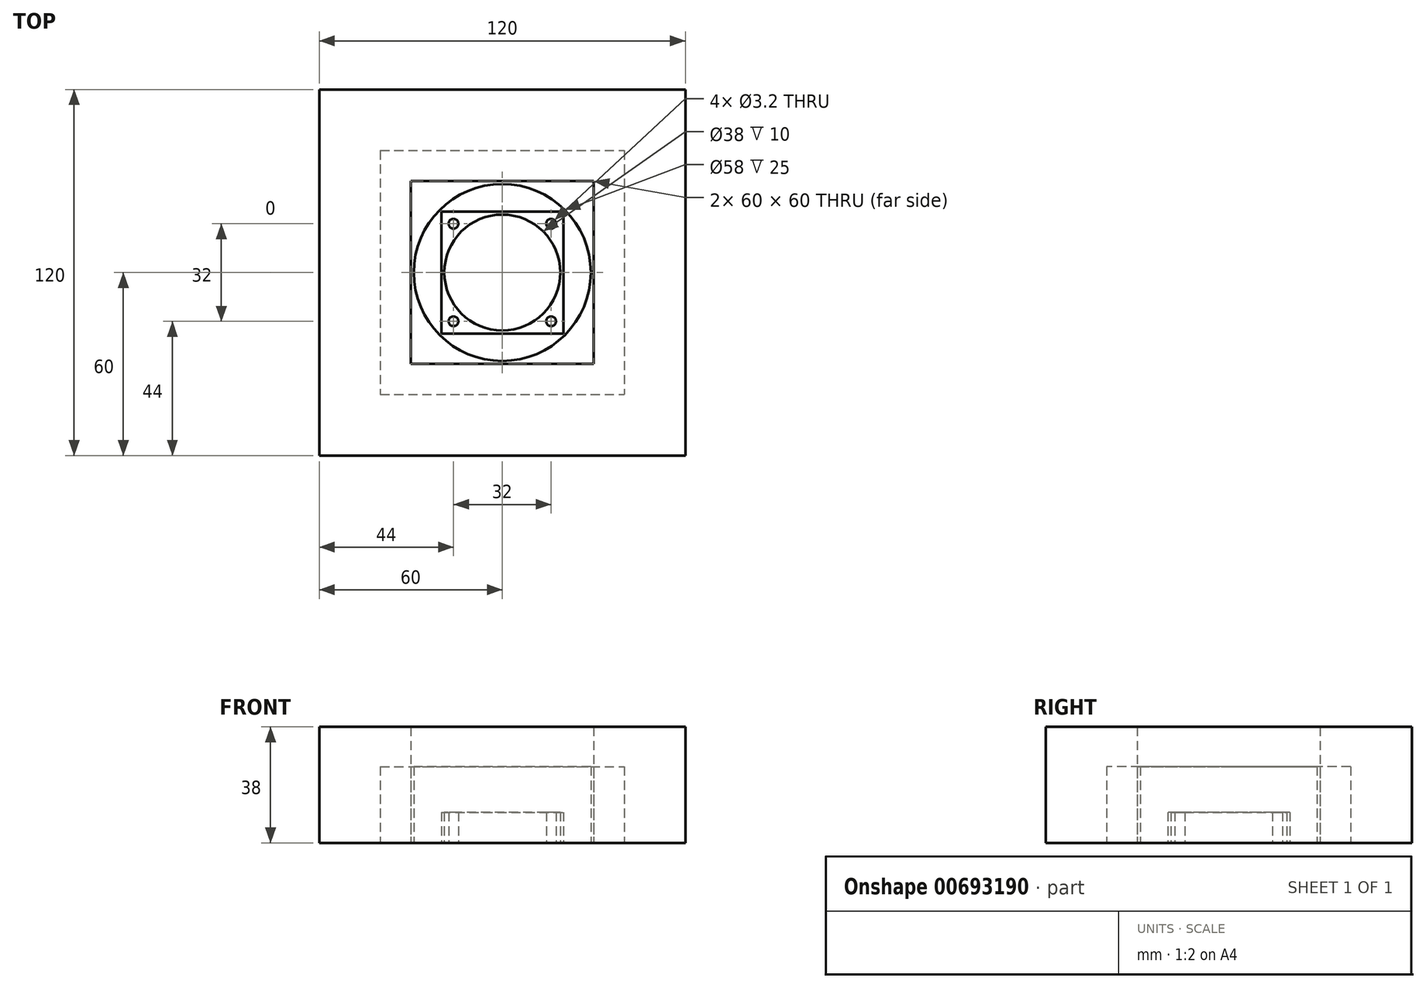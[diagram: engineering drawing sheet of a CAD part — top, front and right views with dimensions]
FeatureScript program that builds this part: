
annotation { "Feature Type Name" : "Feature", "Feature Type Description" : "" }
export const myFeature = defineFeature(function(context is Context, id is Id, definition is map)
    precondition{}
    {
        {
            var Q0;
            Q0=qCreatedBy(makeId("Top.planeOp"),FACE);
            var sketch = newSketch(context, id + "F0", { "sketchPlane" : qUnion([Q0])});
            skLineSegment(sketch, "E0.bottom", {"start": v(-60, 60) * mm, "end": v(60, 60) * mm});
            skLineSegment(sketch, "E0.top", {"start": v(-60, -60) * mm, "end": v(60, -60) * mm});
            skLineSegment(sketch, "E0.left", {"start": v(-60, 60) * mm, "end": v(-60, -60) * mm});
            skLineSegment(sketch, "E0.right", {"start": v(60, 60) * mm, "end": v(60, -60) * mm});
            skLineSegment(sketch, "E1.bottom", {"start": v(-40, 40) * mm, "end": v(40, 40) * mm});
            skLineSegment(sketch, "E1.top", {"start": v(-40, -40) * mm, "end": v(40, -40) * mm});
            skLineSegment(sketch, "E1.left", {"start": v(-40, 40) * mm, "end": v(-40, -40) * mm});
            skLineSegment(sketch, "E1.right", {"start": v(40, 40) * mm, "end": v(40, -40) * mm});
            skLineSegment(sketch, "E2.bottom", {"start": v(-30, -30) * mm, "end": v(30, -30) * mm});
            skLineSegment(sketch, "E2.top", {"start": v(-30, 30) * mm, "end": v(30, 30) * mm});
            skLineSegment(sketch, "E2.left", {"start": v(-30, -30) * mm, "end": v(-30, 30) * mm});
            skLineSegment(sketch, "E2.right", {"start": v(30, -30) * mm, "end": v(30, 30) * mm});
            skCircle(sketch, "E3", {"center": v(0, 0) * mm, "radius": 29 * mm});
            skLineSegment(sketch, "E4.bottom", {"start": v(-20, 20) * mm, "end": v(20, 20) * mm});
            skLineSegment(sketch, "E4.top", {"start": v(-20, -20) * mm, "end": v(20, -20) * mm});
            skLineSegment(sketch, "E4.left", {"start": v(-20, 20) * mm, "end": v(-20, -20) * mm});
            skLineSegment(sketch, "E4.right", {"start": v(20, 20) * mm, "end": v(20, -20) * mm});
            skCircle(sketch, "E5", {"center": v(0, 0) * mm, "radius": 19 * mm});
            skPoint(sketch, "E6", {"position": v(16, 16) * mm});
            skPoint(sketch, "E7", {"position": v(-16, -16) * mm});
            skPoint(sketch, "E8", {"position": v(-16, 16) * mm});
            skPoint(sketch, "E9", {"position": v(16, -16) * mm});
            skSolve(sketch);
        }
        {
            var Q0;
            Q0=makeQuery(id+"F0.imprint","IMPRINT",FACE,{"disambiguationData":[TD([[makeQuery(id+"F0.imprint","IMPRINT",EDGE,{"derivedFrom":sQuery(id+"F0.wireOp",EDGE,"E0.bottom")}),-1.0]])]});
            var Q1;
            Q1=makeQuery(id+"F0.imprint","IMPRINT",FACE,{"disambiguationData":[TD([[makeQuery(id+"F0.imprint","IMPRINT",EDGE,{"derivedFrom":sQuery(id+"F0.wireOp",EDGE,"E1.bottom")}),-1.0]])]});
            extrude(context, id + "F1", {"entities" : qUnion([Q0, Q1]), "depth" : 38 * mm, "offsetDistance" : 25 * mm});
        }
        {
            var Q0;
            Q0=makeQuery(id+"F0.imprint","IMPRINT",FACE,{"disambiguationData":[TD([[makeQuery(id+"F0.imprint","IMPRINT",EDGE,{"derivedFrom":sQuery(id+"F0.wireOp",EDGE,"E1.bottom")}),-1.0]])]});
            extrude(context, id + "F2", {"entities" : qUnion([Q0]), "depth" : 25 * mm, "offsetDistance" : 25 * mm});
        }
        {
            var Q0;
            Q0=makeQuery(id+"F0.imprint","IMPRINT",FACE,{"disambiguationData":[TD([[makeQuery(id+"F0.imprint","IMPRINT",EDGE,{"derivedFrom":sQuery(id+"F0.wireOp",EDGE,"E2.bottom")}),1.0]])]});
            extrude(context, id + "F3", {"entities" : qUnion([Q0]), "depth" : 25 * mm, "offsetDistance" : 25 * mm});
        }
        {
            var Q0;
            Q0=makeQuery(id+"F0.imprint","IMPRINT",FACE,{"disambiguationData":[TD([[makeQuery(id+"F0.imprint","IMPRINT",EDGE,{"derivedFrom":sQuery(id+"F0.wireOp",EDGE,"E4.bottom")}),-1.0]])]});
            extrude(context, id + "F4", {"entities" : qUnion([Q0]), "depth" : 10 * mm, "offsetDistance" : 25 * mm});
        }
        {
            var Q0;
            Q0=sQuery(id+"F0.wireOp",VERTEX,"E8");
            var Q1;
            Q1=sQuery(id+"F0.wireOp",VERTEX,"E6");
            var Q2;
            Q2=sQuery(id+"F0.wireOp",VERTEX,"E9");
            var Q3;
            Q3=sQuery(id+"F0.wireOp",VERTEX,"E7");
            var Q4;
            Q4=makeQuery(id+"F4.opExtrude","SWEPT_BODY",BODY,{"disambiguationData":[OSD([sQuery(id+"F0.wireOp",EDGE,"E4.bottom"),sQuery(id+"F0.wireOp",EDGE,"E4.top"),sQuery(id+"F0.wireOp",EDGE,"E4.left"),sQuery(id+"F0.wireOp",EDGE,"E4.right"),sQuery(id+"F0.wireOp",EDGE,"E5")])]});
            hole(context, id + "F5", {"style" : HoleStyle.SIMPLE, "endStyle" : HoleEndStyle.THROUGH, "oppositeDirection" : true, "holeDiameter" : 3.2 * mm, "majorDiameter" : 5 * mm, "isTappedThrough" : true, "tappedDepth" : 12 * mm, "tapClearance" : 3, "startFromSketch" : true, "locations" : qUnion([Q0, Q1, Q2, Q3]), "scope" : qUnion([Q4])});
        }
    });
